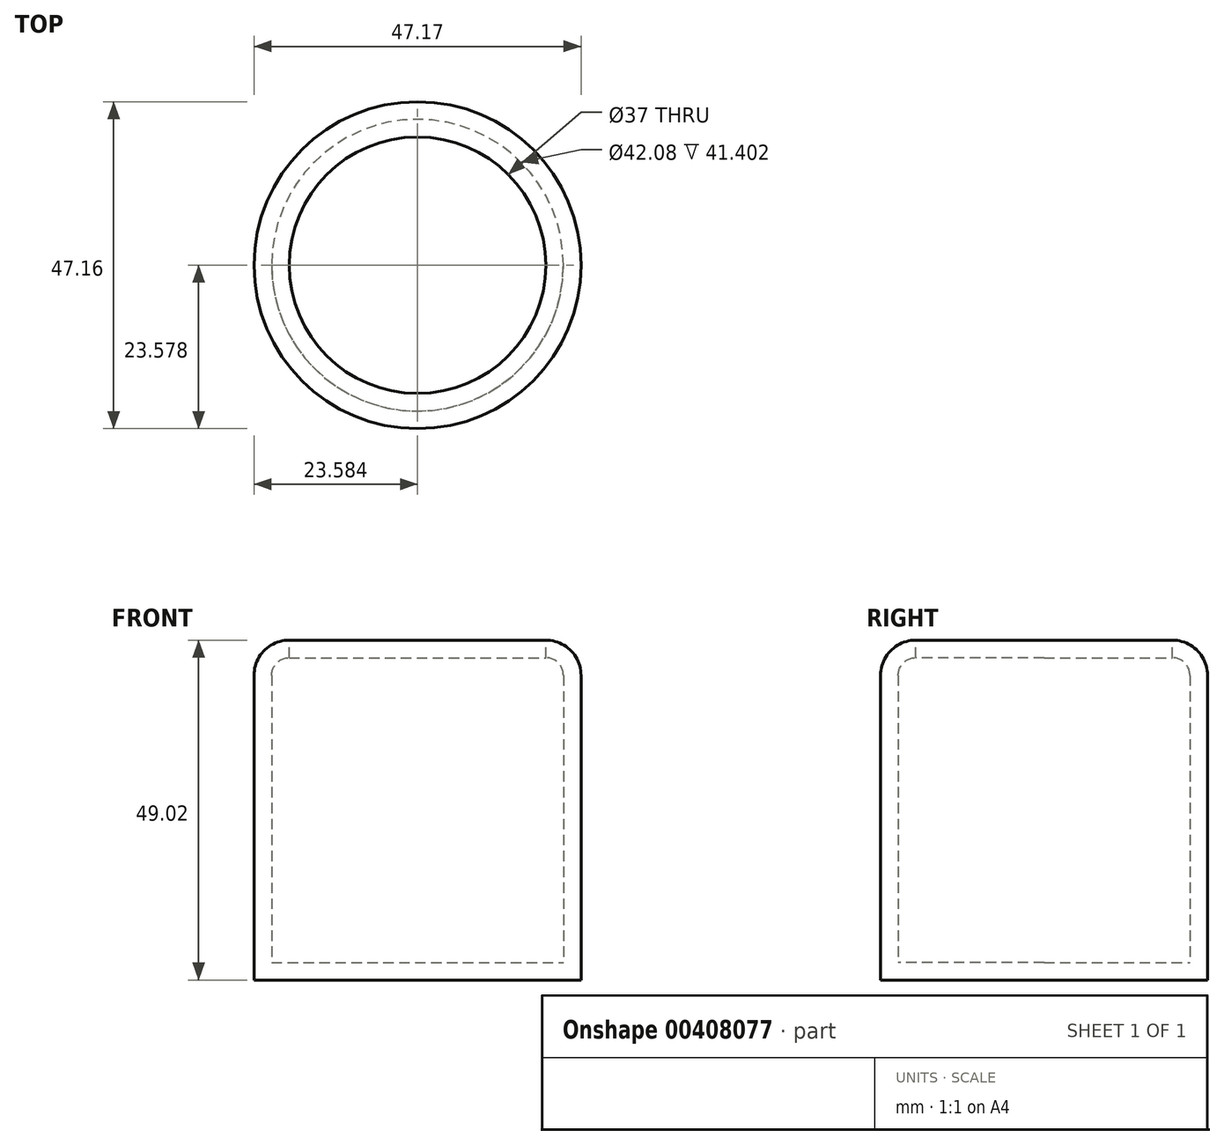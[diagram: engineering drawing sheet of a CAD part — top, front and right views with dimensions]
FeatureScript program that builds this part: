
annotation { "Feature Type Name" : "Feature", "Feature Type Description" : "" }
export const myFeature = defineFeature(function(context is Context, id is Id, definition is map)
    precondition{}
    {
        {
            var Q0;
            Q0=qCreatedBy(makeId("Top.planeOp"),FACE);
            var sketch = newSketch(context, id + "F0", { "sketchPlane" : qUnion([Q0])});
            skCircle(sketch, "E0", {"center": v(-6.1, 30.33) * mm, "radius": 23.58 * mm});
            skSolve(sketch);
        }
        {
            var Q0;
            Q0 = qSketchRegion(id + "F0", true);
            extrude(context, id + "F1", {"entities" : qUnion([Q0]), "depth" : 49.02 * mm});
        }
        {
            var Q0;
            Q0=makeQuery(id+"F1.opExtrude","CAP_EDGE",EDGE,{"disambiguationData":[OSD([sQuery(id+"F0.wireOp",EDGE,"E0")])],"isStart":false});
            fillet(context, id + "F2", {"entities" : qUnion([Q0]), "radius" : 5.08 * mm, "tangentPropagation" : true, "allowEdgeOverflow" : false});
        }
        {
            var Q0;
            Q0=makeQuery(id+"F1.opExtrude","CAP_FACE",FACE,{"disambiguationData":[OSD([sQuery(id+"F0.wireOp",EDGE,"E0")])],"isStart":false});
            shell(context, id + "F3", {"entities" : qUnion([Q0]), "thickness" : 2.54 * mm});
        }
    });
